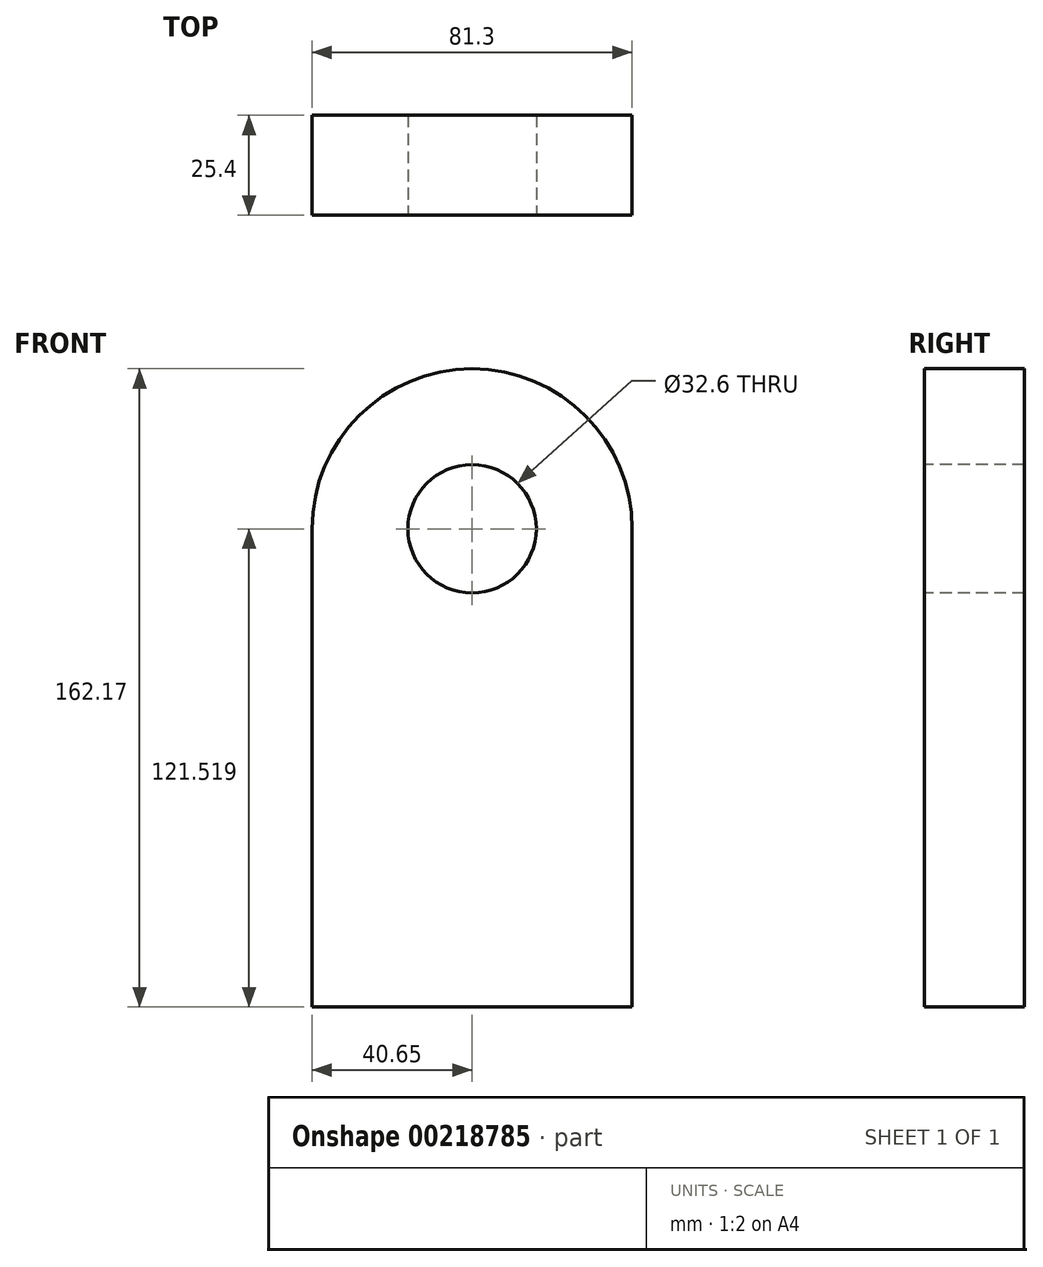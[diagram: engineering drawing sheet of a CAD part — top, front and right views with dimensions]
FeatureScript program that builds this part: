
annotation { "Feature Type Name" : "Feature", "Feature Type Description" : "" }
export const myFeature = defineFeature(function(context is Context, id is Id, definition is map)
    precondition{}
    {
        {
            var Q0;
            Q0=qCreatedBy(makeId("Front.planeOp"),FACE);
            var sketch = newSketch(context, id + "F0", { "sketchPlane" : qUnion([Q0])});
            skLineSegment(sketch, "E0.top", {"start": v(-40.65, -60.76) * mm, "end": v(40.65, -60.76) * mm});
            skLineSegment(sketch, "E0.left", {"start": v(-40.65, 60.76) * mm, "end": v(-40.65, -60.76) * mm});
            skLineSegment(sketch, "E0.right", {"start": v(40.65, 60.76) * mm, "end": v(40.65, -60.76) * mm});
            skPoint(sketch, "E0.middle", {"position": v(0, 0) * mm});
            skArc(sketch, "E1", {"start": v(40.65, 60.76) * mm, "mid": v(0, 101.4) * mm, "end": v(-40.65, 60.76) * mm});
            skCircle(sketch, "E2", {"center": v(0, 60.76) * mm, "radius": 16.3 * mm});
            skSolve(sketch);
        }
        {
            var Q0;
            Q0=makeQuery(id+"F0.imprint","IMPRINT",FACE,{"disambiguationData":[TD([[makeQuery(id+"F0.imprint","IMPRINT",EDGE,{"derivedFrom":sQuery(id+"F0.wireOp",EDGE,"E0.top")}),1.0]])]});
            extrude(context, id + "F1", {"entities" : qUnion([Q0]), "oppositeDirection" : true, "depth" : 25.4 * mm});
        }
    });
